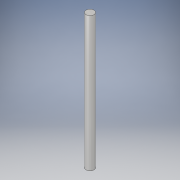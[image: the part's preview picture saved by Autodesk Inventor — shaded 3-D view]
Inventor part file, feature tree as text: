
AUTODESK INVENTOR PART (.ipt)
format: ipt  version: 2017 (Build 210142000, 142)  size: 92,160 bytes
history: native  units: in
note: dims shown in document units (in); Inventor stores cm internally (conversion verified against a paired STEP export)
features: extrude x1, sketch x1
ambient origin geometry x8: Origin, YZ Plane, XZ Plane, XY Plane, X Axis, Y Axis, Z Axis, Center Point
bodies: Solid1 (feature_tree)
feature tree (2):
  extrude  "Extrusion1"  [1 undecoded]
  sketch  "Sketch1"  dims[d1=2.0in d2=0.0in]
note: 1 required parameter value undecoded (feature->parameter linkage not recoverable at this tier; creation-order binding heuristic only, values carry confidence <= 0.55)
